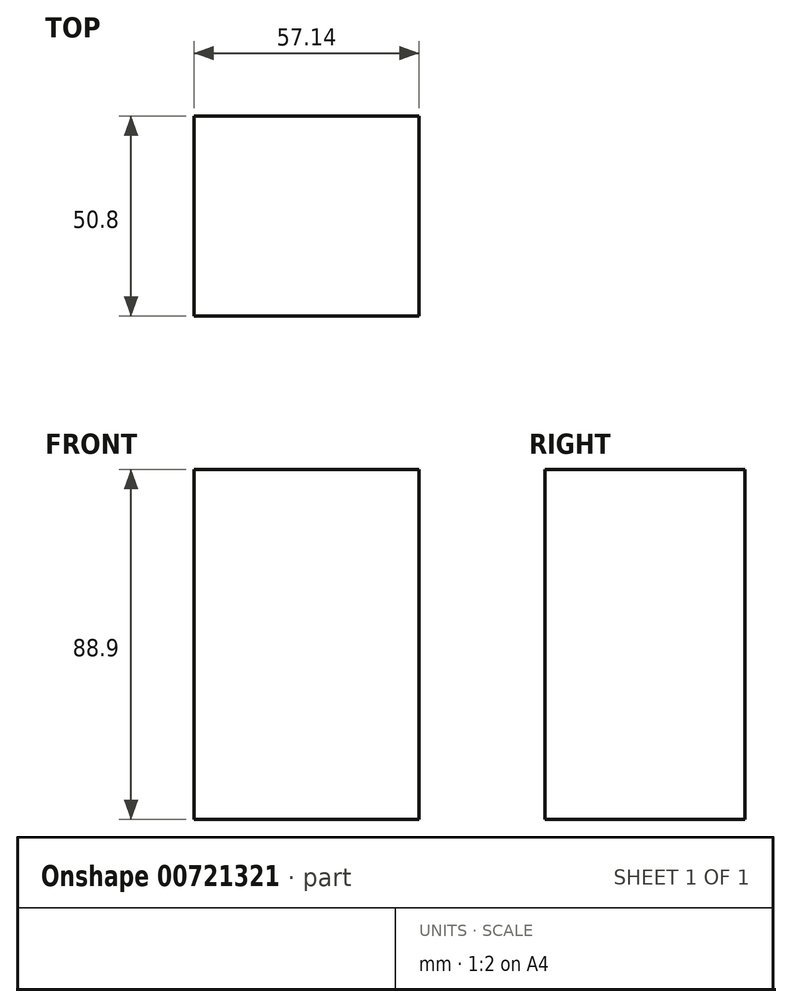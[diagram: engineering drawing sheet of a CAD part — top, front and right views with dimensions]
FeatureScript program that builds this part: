
annotation { "Feature Type Name" : "Feature", "Feature Type Description" : "" }
export const myFeature = defineFeature(function(context is Context, id is Id, definition is map)
    precondition{}
    {
        {
            var Q0;
            Q0=qCreatedBy(makeId("Top.planeOp"),FACE);
            var sketch = newSketch(context, id + "F0", { "sketchPlane" : qUnion([Q0])});
            skLineSegment(sketch, "E0.bottom", {"start": v(28.57, 25.4) * mm, "end": v(-28.58, 25.4) * mm});
            skLineSegment(sketch, "E0.top", {"start": v(28.58, -25.4) * mm, "end": v(-28.57, -25.4) * mm});
            skLineSegment(sketch, "E0.left", {"start": v(28.57, 25.4) * mm, "end": v(28.58, -25.4) * mm});
            skLineSegment(sketch, "E0.right", {"start": v(-28.58, 25.4) * mm, "end": v(-28.57, -25.4) * mm});
            skPoint(sketch, "E0.middle", {"position": v(0, 0) * mm});
            skSolve(sketch);
        }
        {
            var Q0;
            Q0=makeQuery(id+"F0.imprint","IMPRINT",FACE,{"disambiguationData":[TD([[makeQuery(id+"F0.imprint","IMPRINT",EDGE,{"derivedFrom":sQuery(id+"F0.wireOp",EDGE,"E0.bottom")}),1.0]])]});
            extrude(context, id + "F1", {"entities" : qUnion([Q0]), "depth" : 88.9 * mm, "offsetDistance" : 25.4 * mm});
        }
    });
